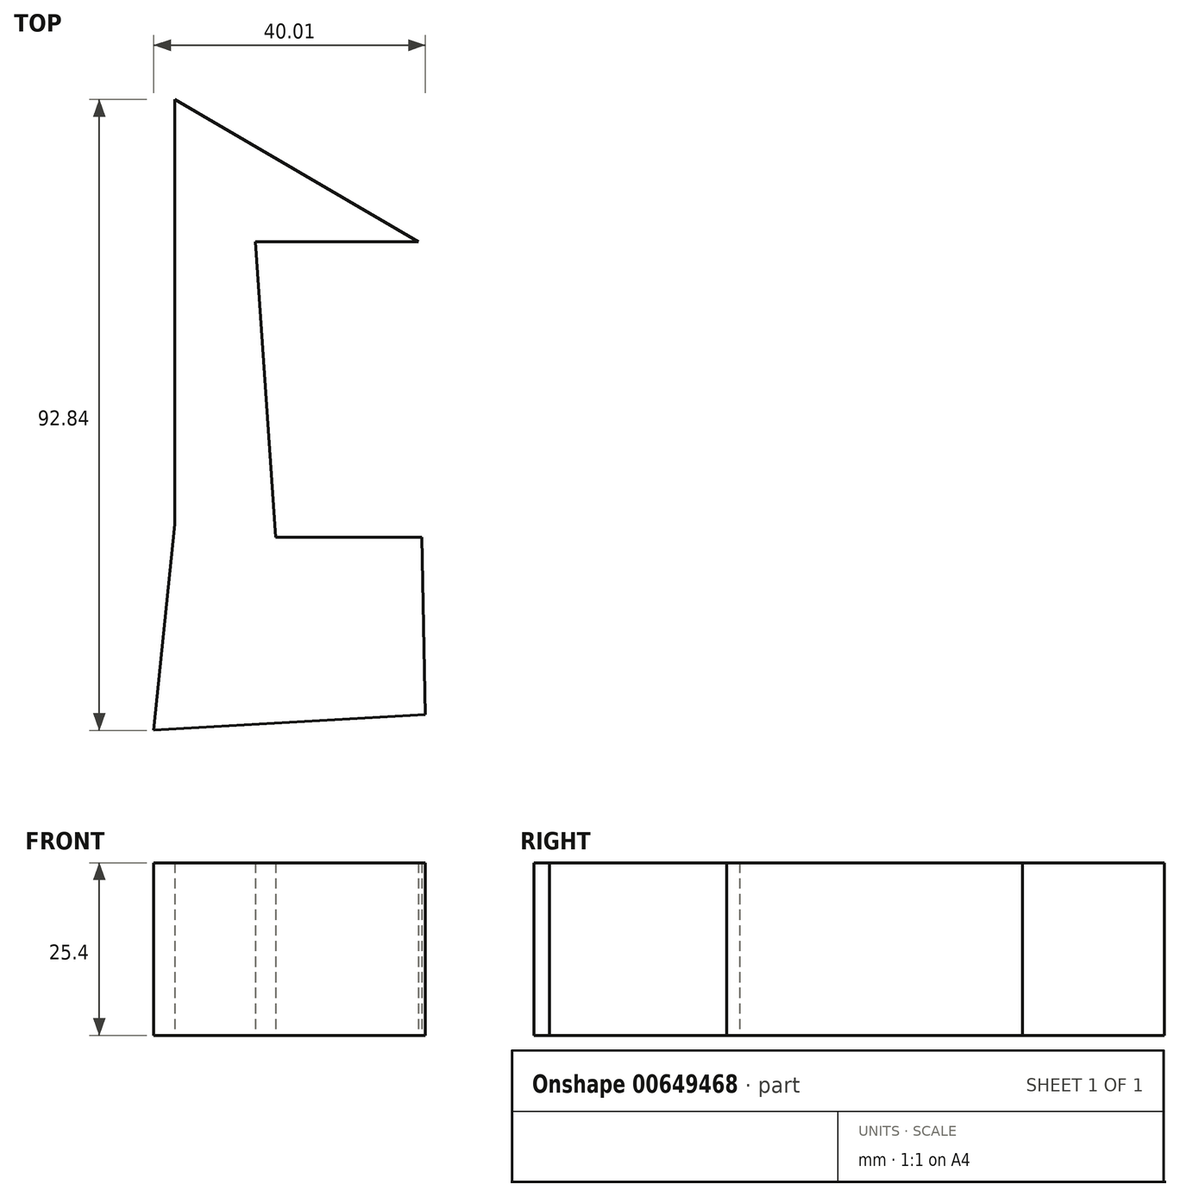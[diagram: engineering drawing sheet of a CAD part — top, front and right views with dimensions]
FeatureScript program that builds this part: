
annotation { "Feature Type Name" : "Feature", "Feature Type Description" : "" }
export const myFeature = defineFeature(function(context is Context, id is Id, definition is map)
    precondition{}
    {
        {
            var Q0;
            Q0=qCreatedBy(makeId("Top.planeOp"),FACE);
            var sketch = newSketch(context, id + "F0", { "sketchPlane" : qUnion([Q0])});
            skLineSegment(sketch, "E0", {"start": v(0, 0) * mm, "end": v(0, 7.76) * mm});
            skLineSegment(sketch, "E1", {"start": v(0, 7.76) * mm, "end": v(0, 62.54) * mm});
            skLineSegment(sketch, "E2", {"start": v(0, 62.54) * mm, "end": v(35.83, 41.63) * mm});
            skLineSegment(sketch, "E3", {"start": v(35.83, 41.63) * mm, "end": v(11.86, 41.63) * mm});
            skLineSegment(sketch, "E4", {"start": v(11.86, 41.63) * mm, "end": v(14.86, -1.91) * mm});
            skLineSegment(sketch, "E5", {"start": v(14.86, -1.91) * mm, "end": v(36.36, -1.91) * mm});
            skLineSegment(sketch, "E6", {"start": v(36.36, -1.91) * mm, "end": v(36.9, -28) * mm});
            skLineSegment(sketch, "E7", {"start": v(36.9, -28) * mm, "end": v(-3.12, -30.3) * mm});
            skLineSegment(sketch, "E8", {"start": v(-3.12, -30.3) * mm, "end": v(0, 0) * mm});
            skLineSegment(sketch, "E9", {"start": v(20.14, -11.26) * mm, "end": v(20.14, -15.15) * mm});
            skPoint(sketch, "E9.endSnap0", {"position": v(-1.56, -15.15) * mm});
            skSolve(sketch);
        }
        {
            var Q0;
            Q0 = qSketchRegion(id + "F0", true);
            extrude(context, id + "F1", {"entities" : qUnion([Q0]), "depth" : 25.4 * mm, "offsetDistance" : 25.4 * mm});
        }
    });
